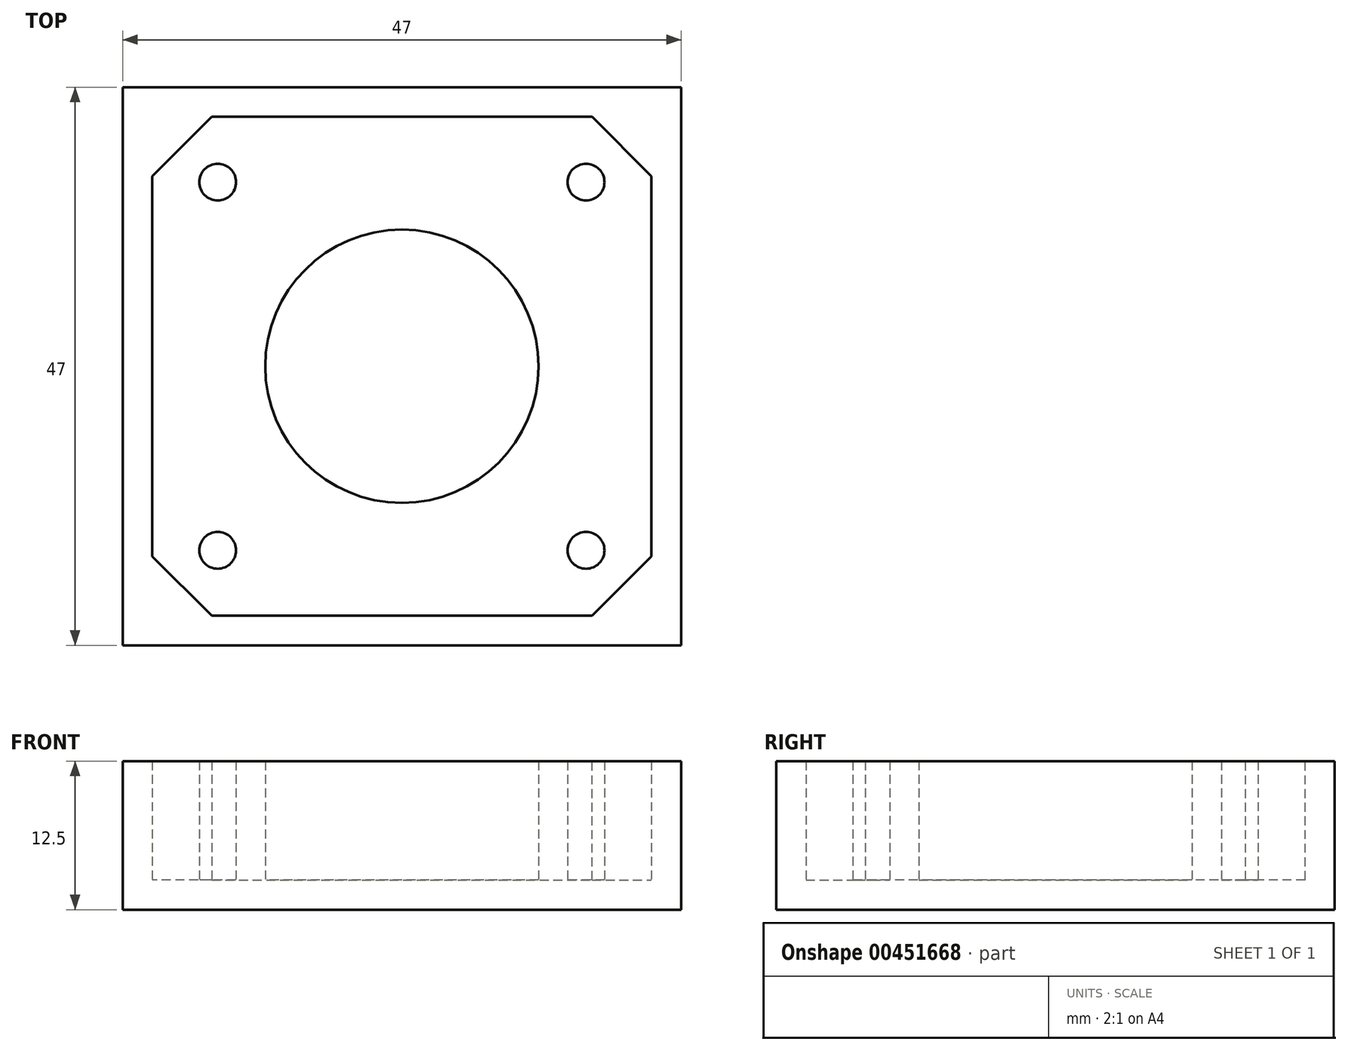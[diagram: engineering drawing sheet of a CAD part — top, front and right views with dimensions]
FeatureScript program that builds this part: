
annotation { "Feature Type Name" : "Feature", "Feature Type Description" : "" }
export const myFeature = defineFeature(function(context is Context, id is Id, definition is map)
    precondition{}
    {
        {
            var Q0;
            Q0=qCreatedBy(makeId("Top.planeOp"),FACE);
            var sketch = newSketch(context, id + "F0", { "sketchPlane" : qUnion([Q0])});
            skLineSegment(sketch, "E0.bottom", {"start": v(-41.82, 29.14) * mm, "end": v(0.18, 29.14) * mm});
            skLineSegment(sketch, "E0.top", {"start": v(-41.82, -12.86) * mm, "end": v(0.18, -12.86) * mm});
            skLineSegment(sketch, "E0.left", {"start": v(-41.82, 29.14) * mm, "end": v(-41.82, -12.86) * mm});
            skLineSegment(sketch, "E0.right", {"start": v(0.18, 29.14) * mm, "end": v(0.18, -12.86) * mm});
            skLineSegment(sketch, "E1", {"start": v(-41.82, 29.14) * mm, "end": v(0.18, -12.86) * mm, "construction": true});
            skCircle(sketch, "E2", {"center": v(-20.82, 8.14) * mm, "radius": 11.5 * mm});
            skLineSegment(sketch, "E3.bottom", {"start": v(-36.32, -7.36) * mm, "end": v(-5.32, -7.36) * mm, "construction": true});
            skLineSegment(sketch, "E3.top", {"start": v(-36.32, 23.64) * mm, "end": v(-5.32, 23.64) * mm, "construction": true});
            skLineSegment(sketch, "E3.left", {"start": v(-36.32, -7.36) * mm, "end": v(-36.32, 23.64) * mm, "construction": true});
            skLineSegment(sketch, "E3.right", {"start": v(-5.32, -7.36) * mm, "end": v(-5.32, 23.64) * mm, "construction": true});
            skCircle(sketch, "E4", {"center": v(-36.32, 23.64) * mm, "radius": 1.55 * mm});
            skCircle(sketch, "E5", {"center": v(-5.32, 23.64) * mm, "radius": 1.55 * mm});
            skCircle(sketch, "E6", {"center": v(-5.32, -7.36) * mm, "radius": 1.55 * mm});
            skCircle(sketch, "E7", {"center": v(-36.32, -7.36) * mm, "radius": 1.55 * mm});
            skSolve(sketch);
        }
        {
            var Q0;
            Q0=makeQuery(id+"F0.imprint","IMPRINT",FACE,{"disambiguationData":[TD([[makeQuery(id+"F0.imprint","IMPRINT",EDGE,{"derivedFrom":sQuery(id+"F0.wireOp",EDGE,"E0.bottom")}),-1.0]])]});
            var Q1;
            Q1=makeQuery(id+"F0.imprint","IMPRINT",FACE,{"disambiguationData":[TD([[makeQuery(id+"F0.imprint","IMPRINT",EDGE,{"derivedFrom":sQuery(id+"F0.wireOp",EDGE,"E2")}),1.0]])]});
            extrude(context, id + "F1", {"entities" : qUnion([Q0, Q1]), "depth" : 10 * mm});
        }
        {
            var Q0;
            Q0=makeQuery(id+"F1.opExtrude","CAP_FACE",FACE,{"disambiguationData":[OSD([sQuery(id+"F0.wireOp",EDGE,"E0.bottom"),sQuery(id+"F0.wireOp",EDGE,"E0.top"),sQuery(id+"F0.wireOp",EDGE,"E0.left"),sQuery(id+"F0.wireOp",EDGE,"E0.right"),sQuery(id+"F0.wireOp",EDGE,"E4"),sQuery(id+"F0.wireOp",EDGE,"E5"),sQuery(id+"F0.wireOp",EDGE,"E6"),sQuery(id+"F0.wireOp",EDGE,"E7")])],"isStart":false});
            shell(context, id + "F2", {"entities" : qUnion([Q0]), "thickness" : 2.5 * mm, "oppositeDirection" : true});
        }
        {
            var Q0;
            Q0=makeQuery(id+"F2.opShell","OFFSET_EDGE",EDGE,{"disambiguationData":[OSD([sQuery(id+"F0.wireOp",EDGE,"E0.bottom"),sQuery(id+"F0.wireOp",EDGE,"E0.left")])]});
            var Q1;
            Q1=makeQuery(id+"F2.opShell","OFFSET_EDGE",EDGE,{"disambiguationData":[OSD([sQuery(id+"F0.wireOp",EDGE,"E0.bottom"),sQuery(id+"F0.wireOp",EDGE,"E0.right")])]});
            var Q2;
            Q2=makeQuery(id+"F2.opShell","OFFSET_EDGE",EDGE,{"disambiguationData":[OSD([sQuery(id+"F0.wireOp",EDGE,"E0.top"),sQuery(id+"F0.wireOp",EDGE,"E0.right")])]});
            var Q3;
            Q3=makeQuery(id+"F2.opShell","OFFSET_EDGE",EDGE,{"disambiguationData":[OSD([sQuery(id+"F0.wireOp",EDGE,"E0.top"),sQuery(id+"F0.wireOp",EDGE,"E0.left")])]});
            chamfer(context, id + "F3", {"entities" : qUnion([Q0, Q1, Q2, Q3]), "width" : 5 * mm, "tangentPropagation" : true});
        }
        {
            var Q0;
            Q0=makeQuery(id+"F0.imprint","IMPRINT",FACE,{"disambiguationData":[TD([[makeQuery(id+"F0.imprint","IMPRINT",EDGE,{"derivedFrom":sQuery(id+"F0.wireOp",EDGE,"E2")}),1.0]])]});
            extrude(context, id + "F4", {"entities" : qUnion([Q0]), "operationType" : NewBodyOperationType.ADD, "depth" : 10 * mm});
        }
    });
